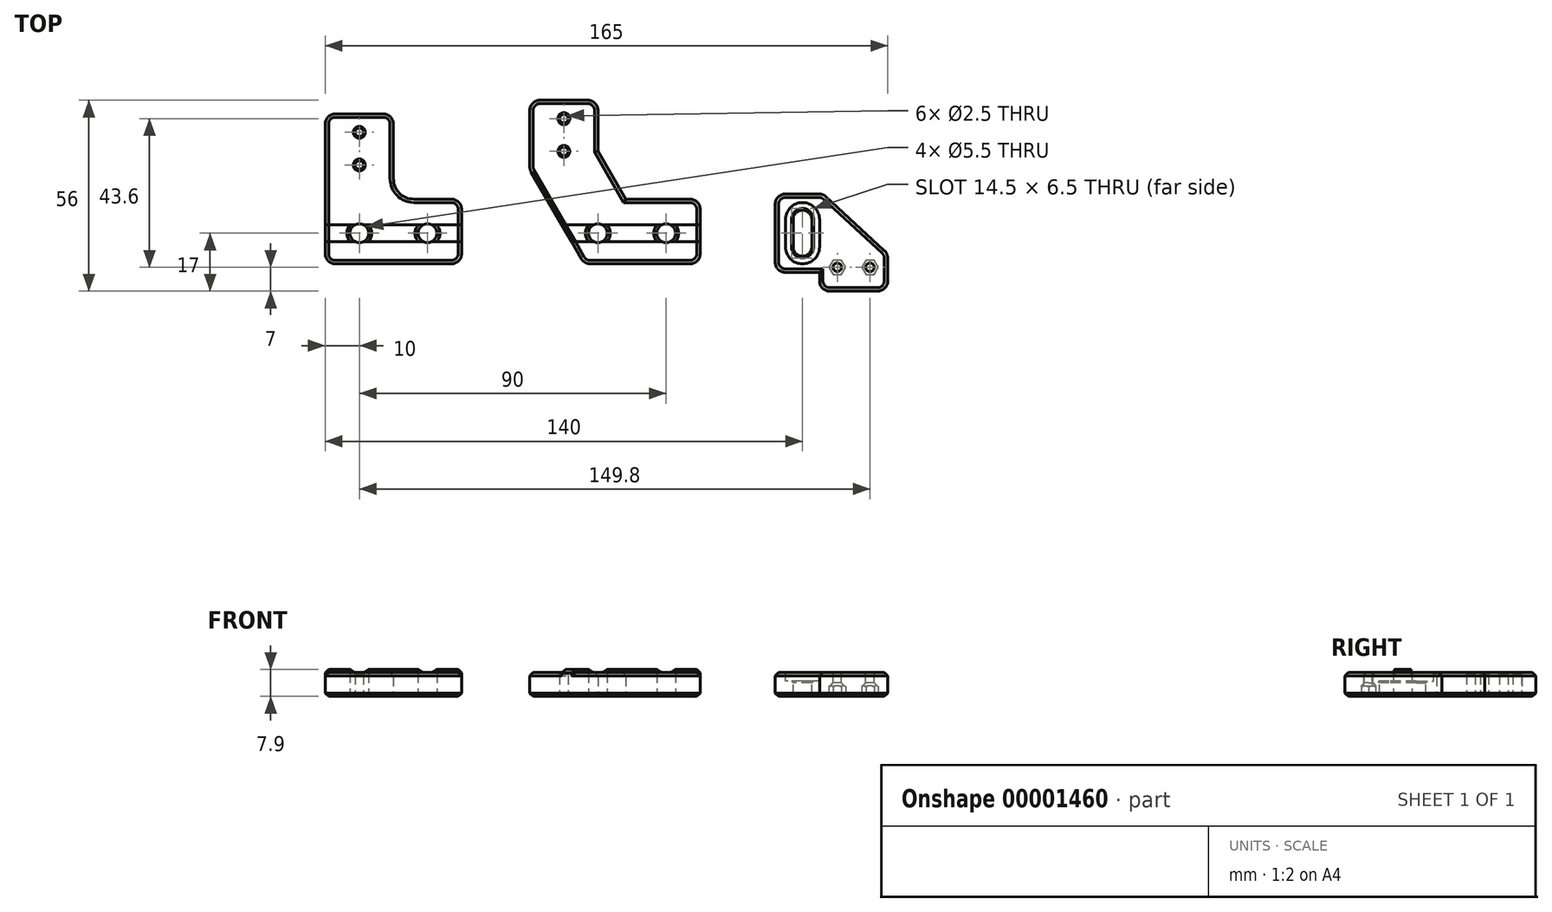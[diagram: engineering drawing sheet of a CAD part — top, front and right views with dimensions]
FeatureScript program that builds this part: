
annotation { "Feature Type Name" : "Feature", "Feature Type Description" : "" }
export const myFeature = defineFeature(function(context is Context, id is Id, definition is map)
    precondition{}
    {
        {
            var Q0;
            Q0=qCreatedBy(makeId("Top.planeOp"),FACE);
            var sketch = newSketch(context, id + "F0", { "sketchPlane" : qUnion([Q0])});
            skLineSegment(sketch, "E0", {"start": v(-8, 11.5) * mm, "end": v(6, 11.5) * mm});
            skLineSegment(sketch, "E1", {"start": v(-8, 11.5) * mm, "end": v(-8, -11.5) * mm});
            skLineSegment(sketch, "E2", {"start": v(5, -11.5) * mm, "end": v(-8, -11.5) * mm});
            skLineSegment(sketch, "E3", {"start": v(5, -11.5) * mm, "end": v(5, -17) * mm});
            skLineSegment(sketch, "E4", {"start": v(25, -17) * mm, "end": v(5, -17) * mm});
            skLineSegment(sketch, "E5", {"start": v(25, -17) * mm, "end": v(25, -6) * mm});
            skLineSegment(sketch, "E6", {"start": v(6, 11.5) * mm, "end": v(25, -6) * mm});
            skLineSegment(sketch, "E7", {"start": v(0, 11.5) * mm, "end": v(0, -11.5) * mm, "construction": true});
            skSolve(sketch);
        }
        {
            var Q0;
            Q0=makeQuery(id+"F0.imprint","IMPRINT",FACE,{"disambiguationData":[TD([[makeQuery(id+"F0.imprint","IMPRINT",EDGE,{"derivedFrom":sQuery(id+"F0.wireOp",EDGE,"E0")}),-1.0]])]});
            extrude(context, id + "F1", {"entities" : qUnion([Q0]), "depth" : 7 * mm});
        }
        {
            var Q0;
            Q0=makeQuery(id+"F1.opExtrude","CAP_FACE",FACE,{"disambiguationData":[OSD([sQuery(id+"F0.wireOp",EDGE,"E0"),sQuery(id+"F0.wireOp",EDGE,"E1"),sQuery(id+"F0.wireOp",EDGE,"E2"),sQuery(id+"F0.wireOp",EDGE,"E3"),sQuery(id+"F0.wireOp",EDGE,"E4"),sQuery(id+"F0.wireOp",EDGE,"E5"),sQuery(id+"F0.wireOp",EDGE,"E6")])],"isStart":false});
            var sketch = newSketch(context, id + "F2", { "sketchPlane" : qUnion([Q0])});
            skLineSegment(sketch, "E8", {"start": v(0, 4) * mm, "end": v(0, -4) * mm, "construction": true});
            skArc(sketch, "E9", {"start": v(2.75, 4) * mm, "mid": v(0, 6.75) * mm, "end": v(-2.75, 4) * mm});
            skArc(sketch, "E10", {"start": v(-2.75, -4) * mm, "mid": v(0, -6.75) * mm, "end": v(2.75, -4) * mm});
            skLineSegment(sketch, "E11", {"start": v(-2.75, 4) * mm, "end": v(-2.75, -4) * mm});
            skLineSegment(sketch, "E12", {"start": v(2.75, 4) * mm, "end": v(2.75, -4) * mm});
            skSolve(sketch);
        }
        {
            var Q0;
            Q0=makeQuery(id+"F2.imprint","IMPRINT",FACE,{"disambiguationData":[TD([[makeQuery(id+"F2.imprint","IMPRINT",EDGE,{"derivedFrom":sQuery(id+"F2.wireOp",EDGE,"E9")}),1.0]])]});
            extrude(context, id + "F3", {"entities" : qUnion([Q0]), "operationType" : NewBodyOperationType.REMOVE, "endBound" : BoundingType.THROUGH_ALL, "oppositeDirection" : true, "depth" : 25 * mm});
        }
        {
            var Q0;
            Q0=makeQuery(id+"F1.opExtrude","CAP_FACE",FACE,{"disambiguationData":[OSD([sQuery(id+"F0.wireOp",EDGE,"E0"),sQuery(id+"F0.wireOp",EDGE,"E1"),sQuery(id+"F0.wireOp",EDGE,"E2"),sQuery(id+"F0.wireOp",EDGE,"E3"),sQuery(id+"F0.wireOp",EDGE,"E4"),sQuery(id+"F0.wireOp",EDGE,"E5"),sQuery(id+"F0.wireOp",EDGE,"E6")])],"isStart":false});
            var sketch = newSketch(context, id + "F4", { "sketchPlane" : qUnion([Q0])});
            skArc(sketch, "E13.0", {"start": v(5, 4) * mm, "mid": v(0, 9) * mm, "end": v(-5, 4) * mm});
            skLineSegment(sketch, "E13.1", {"start": v(5, 4) * mm, "end": v(5, -4) * mm});
            skArc(sketch, "E13.2", {"start": v(-5, -4) * mm, "mid": v(0, -9) * mm, "end": v(5, -4) * mm});
            skLineSegment(sketch, "E13.3", {"start": v(-5, 4) * mm, "end": v(-5, -4) * mm});
            skSolve(sketch);
        }
        {
            var Q0;
            {var subQ3=makeQuery(id+"F4.imprint","IMPRINT",EDGE,{"derivedFrom":makeQuery(id+"F3.boolean.opBoolean","COPY",EDGE,{"derivedFrom":makeQuery(id+"F3.opExtrude","CAP_EDGE",EDGE,{"disambiguationData":[OSD([sQuery(id+"F2.wireOp",EDGE,"E9")])],"isStart":true})})});Q0=qUnion([makeQuery(id+"F4.imprint","IMPRINT",FACE,{"disambiguationData":[TD([[subQ3,1.0]])]}),makeQuery(id+"F4.imprint","IMPRINT",FACE,{"disambiguationData":[TD([[makeQuery(id+"F4.imprint","IMPRINT",EDGE,{"derivedFrom":sQuery(id+"F4.wireOp",EDGE,"E13.0")}),1.0]])]})]);}
            extrude(context, id + "F5", {"entities" : qUnion([Q0]), "operationType" : NewBodyOperationType.REMOVE, "oppositeDirection" : true, "depth" : 2.5 * mm});
        }
        {
            var Q0;
            Q0=makeQuery(id+"F1.opExtrude","CAP_FACE",FACE,{"disambiguationData":[OSD([sQuery(id+"F0.wireOp",EDGE,"E0"),sQuery(id+"F0.wireOp",EDGE,"E1"),sQuery(id+"F0.wireOp",EDGE,"E2"),sQuery(id+"F0.wireOp",EDGE,"E3"),sQuery(id+"F0.wireOp",EDGE,"E4"),sQuery(id+"F0.wireOp",EDGE,"E5"),sQuery(id+"F0.wireOp",EDGE,"E6")])],"isStart":false});
            var sketch = newSketch(context, id + "F6", { "sketchPlane" : qUnion([Q0])});
            skCircle(sketch, "E14", {"center": v(10.2, -10) * mm, "radius": 1.25 * mm});
            skLineSegment(sketch, "E15", {"start": v(10.2, -10) * mm, "end": v(19.8, -10) * mm, "construction": true});
            skCircle(sketch, "E16", {"center": v(19.8, -10) * mm, "radius": 1.25 * mm});
            skLineSegment(sketch, "E17", {"start": v(15, -10) * mm, "end": v(15, -17) * mm, "construction": true});
            skSolve(sketch);
        }
        {
            var Q0;
            {Q0=qUnion([makeQuery(id+"F6.imprint","IMPRINT",FACE,{"disambiguationData":[TD([[makeQuery(id+"F6.imprint","IMPRINT",EDGE,{"derivedFrom":sQuery(id+"F6.wireOp",EDGE,"E14")}),1.0]])]}),makeQuery(id+"F6.imprint","IMPRINT",FACE,{"disambiguationData":[TD([[makeQuery(id+"F6.imprint","IMPRINT",EDGE,{"derivedFrom":sQuery(id+"F6.wireOp",EDGE,"E16")}),1.0]])]})]);}
            extrude(context, id + "F7", {"entities" : qUnion([Q0]), "operationType" : NewBodyOperationType.REMOVE, "endBound" : BoundingType.THROUGH_ALL, "oppositeDirection" : true, "depth" : 25 * mm});
        }
        {
            var Q0;
            Q0=makeQuery(id+"F1.opExtrude","SWEPT_EDGE",EDGE,{"disambiguationData":[OSD([sQuery(id+"F0.wireOp",EDGE,"E1"),sQuery(id+"F0.wireOp",EDGE,"E2")])]});
            var Q1;
            Q1=makeQuery(id+"F1.opExtrude","SWEPT_EDGE",EDGE,{"disambiguationData":[OSD([sQuery(id+"F0.wireOp",EDGE,"E3"),sQuery(id+"F0.wireOp",EDGE,"E4")])]});
            var Q2;
            Q2=makeQuery(id+"F1.opExtrude","SWEPT_EDGE",EDGE,{"disambiguationData":[OSD([sQuery(id+"F0.wireOp",EDGE,"E4"),sQuery(id+"F0.wireOp",EDGE,"E5")])]});
            var Q3;
            Q3=makeQuery(id+"F1.opExtrude","SWEPT_EDGE",EDGE,{"disambiguationData":[OSD([sQuery(id+"F0.wireOp",EDGE,"E5"),sQuery(id+"F0.wireOp",EDGE,"E6")])]});
            var Q4;
            Q4=makeQuery(id+"F1.opExtrude","SWEPT_EDGE",EDGE,{"disambiguationData":[OSD([sQuery(id+"F0.wireOp",EDGE,"E0"),sQuery(id+"F0.wireOp",EDGE,"E6")])]});
            var Q5;
            Q5=makeQuery(id+"F1.opExtrude","SWEPT_EDGE",EDGE,{"disambiguationData":[OSD([sQuery(id+"F0.wireOp",EDGE,"E0"),sQuery(id+"F0.wireOp",EDGE,"E1")])]});
            fillet(context, id + "F8", {"entities" : qUnion([Q0, Q1, Q2, Q3, Q4, Q5]), "radius" : 3 * mm, "tangentPropagation" : true, "allowEdgeOverflow" : false});
        }
        {
            var Q0;
            Q0=makeQuery(id+"F1.opExtrude","SWEPT_BODY",BODY,{"disambiguationData":[OSD([sQuery(id+"F0.wireOp",EDGE,"E0"),sQuery(id+"F0.wireOp",EDGE,"E1"),sQuery(id+"F0.wireOp",EDGE,"E2"),sQuery(id+"F0.wireOp",EDGE,"E3"),sQuery(id+"F0.wireOp",EDGE,"E4"),sQuery(id+"F0.wireOp",EDGE,"E5"),sQuery(id+"F0.wireOp",EDGE,"E6")])]});
            transform(context, id + "F9", {"entities" : qUnion([Q0]), "transformType" : TransformType.TRANSLATION_3D, "dx" : 50 * mm, "dy" : 0 * mm, "dz" : 0 * mm, "makeCopy" : false});
        }
        {
            var Q0;
            Q0=qCreatedBy(makeId("Top.planeOp"),FACE);
            var sketch = newSketch(context, id + "F10", { "sketchPlane" : qUnion([Q0])});
            skLineSegment(sketch, "E18", {"start": v(20, -9) * mm, "end": v(20, 10) * mm});
            skLineSegment(sketch, "E19", {"start": v(20, 10) * mm, "end": v(-1.88, 10) * mm});
            skLineSegment(sketch, "E20", {"start": v(-1.88, 10) * mm, "end": v(-10, 24.07) * mm});
            skLineSegment(sketch, "E21", {"start": v(-10, 24.07) * mm, "end": v(-10, 39) * mm});
            skLineSegment(sketch, "E22", {"start": v(-10, 39) * mm, "end": v(-30, 39) * mm});
            skLineSegment(sketch, "E23", {"start": v(-30, 39) * mm, "end": v(-30, 18.71) * mm});
            skLineSegment(sketch, "E24", {"start": v(-30, 18.71) * mm, "end": v(-14, -9) * mm});
            skLineSegment(sketch, "E25", {"start": v(-14, -9) * mm, "end": v(20, -9) * mm});
            skLineSegment(sketch, "E26", {"start": v(-10, 0) * mm, "end": v(10, 0) * mm, "construction": true});
            skSolve(sketch);
        }
        {
            var Q0;
            Q0=makeQuery(id+"F10.imprint","IMPRINT",FACE,{"disambiguationData":[TD([[makeQuery(id+"F10.imprint","IMPRINT",EDGE,{"derivedFrom":sQuery(id+"F10.wireOp",EDGE,"E18")}),1.0]])]});
            extrude(context, id + "F11", {"entities" : qUnion([Q0]), "depth" : 7 * mm});
        }
        {
            var Q0;
            Q0=makeQuery(id+"F11.opExtrude","SWEPT_FACE",FACE,{"disambiguationData":[OSD([sQuery(id+"F10.wireOp",EDGE,"E18")])]});
            var sketch = newSketch(context, id + "F12", { "sketchPlane" : qUnion([Q0])});
            skLineSegment(sketch, "E27", {"start": v(0, 0) * mm, "end": v(0, 7.45) * mm, "construction": true});
            skLineSegment(sketch, "E28.rect.bottom", {"start": v(2.5, 7) * mm, "end": v(-2.5, 7) * mm});
            skLineSegment(sketch, "E28.rect.top", {"start": v(2.5, 7.9) * mm, "end": v(-2.5, 7.9) * mm});
            skLineSegment(sketch, "E28.rect.left", {"start": v(2.5, 7) * mm, "end": v(2.5, 7.9) * mm});
            skLineSegment(sketch, "E28.rect.right", {"start": v(-2.5, 7) * mm, "end": v(-2.5, 7.9) * mm});
            skPoint(sketch, "E28.rect.middle", {"position": v(0, 7.45) * mm});
            skSolve(sketch);
        }
        {
            var Q0;
            Q0=makeQuery(id+"F12.imprint","IMPRINT",FACE,{"disambiguationData":[TD([[makeQuery(id+"F12.imprint","IMPRINT",EDGE,{"derivedFrom":sQuery(id+"F12.wireOp",EDGE,"E28.rect.bottom")}),1.0]])]});
            var Q1;
            Q1=makeQuery(id+"F11.opExtrude","SWEPT_FACE",FACE,{"disambiguationData":[OSD([sQuery(id+"F10.wireOp",EDGE,"E24")])]});
            extrude(context, id + "F13", {"entities" : qUnion([Q0]), "operationType" : NewBodyOperationType.ADD, "endBound" : BoundingType.UP_TO_SURFACE, "oppositeDirection" : true, "endBoundEntityFace" : qUnion([Q1]), "depth" : 25 * mm});
        }
        {
            var Q0;
            Q0=makeQuery(id+"F11.opExtrude","CAP_FACE",FACE,{"disambiguationData":[OSD([sQuery(id+"F10.wireOp",EDGE,"E18"),sQuery(id+"F10.wireOp",EDGE,"E19"),sQuery(id+"F10.wireOp",EDGE,"E20"),sQuery(id+"F10.wireOp",EDGE,"E21"),sQuery(id+"F10.wireOp",EDGE,"E22"),sQuery(id+"F10.wireOp",EDGE,"E23"),sQuery(id+"F10.wireOp",EDGE,"E24"),sQuery(id+"F10.wireOp",EDGE,"E25")])],"isStart":true});
            var sketch = newSketch(context, id + "F14", { "sketchPlane" : qUnion([Q0])});
            skLineSegment(sketch, "E29", {"start": v(-10, 0) * mm, "end": v(10, 0) * mm, "construction": true});
            skCircle(sketch, "E30", {"center": v(-10, 0) * mm, "radius": 2.75 * mm});
            skCircle(sketch, "E31", {"center": v(10, 0) * mm, "radius": 2.75 * mm});
            skLineSegment(sketch, "E32", {"start": v(-20, -24) * mm, "end": v(-20, -33.6) * mm, "construction": true});
            skCircle(sketch, "E33", {"center": v(-20, -33.6) * mm, "radius": 1.25 * mm});
            skCircle(sketch, "E34", {"center": v(-20, -24) * mm, "radius": 1.25 * mm});
            skLineSegment(sketch, "E35", {"start": v(-20, -39) * mm, "end": v(-20, -33.6) * mm, "construction": true});
            skLineSegment(sketch, "E36", {"start": v(-20, -28.8) * mm, "end": v(-30, -28.8) * mm, "construction": true});
            skSolve(sketch);
        }
        {
            var Q0;
            {Q0=qUnion([makeQuery(id+"F14.imprint","IMPRINT",FACE,{"disambiguationData":[TD([[makeQuery(id+"F14.imprint","IMPRINT",EDGE,{"derivedFrom":sQuery(id+"F14.wireOp",EDGE,"E30")}),1.0]])]}),makeQuery(id+"F14.imprint","IMPRINT",FACE,{"disambiguationData":[TD([[makeQuery(id+"F14.imprint","IMPRINT",EDGE,{"derivedFrom":sQuery(id+"F14.wireOp",EDGE,"E31")}),1.0]])]}),makeQuery(id+"F14.imprint","IMPRINT",FACE,{"disambiguationData":[TD([[makeQuery(id+"F14.imprint","IMPRINT",EDGE,{"derivedFrom":sQuery(id+"F14.wireOp",EDGE,"E33")}),1.0]])]}),makeQuery(id+"F14.imprint","IMPRINT",FACE,{"disambiguationData":[TD([[makeQuery(id+"F14.imprint","IMPRINT",EDGE,{"derivedFrom":sQuery(id+"F14.wireOp",EDGE,"E34")}),1.0]])]})]);}
            extrude(context, id + "F15", {"entities" : qUnion([Q0]), "operationType" : NewBodyOperationType.REMOVE, "endBound" : BoundingType.THROUGH_ALL, "oppositeDirection" : true, "depth" : 25 * mm});
        }
        {
            var Q0;
            Q0=makeQuery(id+"F11.opExtrude","SWEPT_EDGE",EDGE,{"disambiguationData":[OSD([sQuery(id+"F10.wireOp",EDGE,"E24"),sQuery(id+"F10.wireOp",EDGE,"E25")])]});
            var Q1;
            Q1=makeQuery(id+"F11.opExtrude","SWEPT_EDGE",EDGE,{"disambiguationData":[OSD([sQuery(id+"F10.wireOp",EDGE,"E23"),sQuery(id+"F10.wireOp",EDGE,"E24")])]});
            var Q2;
            Q2=makeQuery(id+"F11.opExtrude","SWEPT_EDGE",EDGE,{"disambiguationData":[OSD([sQuery(id+"F10.wireOp",EDGE,"E22"),sQuery(id+"F10.wireOp",EDGE,"E23")])]});
            var Q3;
            Q3=makeQuery(id+"F11.opExtrude","SWEPT_EDGE",EDGE,{"disambiguationData":[OSD([sQuery(id+"F10.wireOp",EDGE,"E21"),sQuery(id+"F10.wireOp",EDGE,"E22")])]});
            var Q4;
            Q4=makeQuery(id+"F11.opExtrude","SWEPT_EDGE",EDGE,{"disambiguationData":[OSD([sQuery(id+"F10.wireOp",EDGE,"E18"),sQuery(id+"F10.wireOp",EDGE,"E19")])]});
            var Q5;
            Q5=makeQuery(id+"F11.opExtrude","SWEPT_EDGE",EDGE,{"disambiguationData":[OSD([sQuery(id+"F10.wireOp",EDGE,"E18"),sQuery(id+"F10.wireOp",EDGE,"E25")])]});
            fillet(context, id + "F16", {"entities" : qUnion([Q0, Q1, Q2, Q3, Q4, Q5]), "radius" : 3 * mm, "tangentPropagation" : true, "allowEdgeOverflow" : false});
        }
        {
            var Q0;
            Q0=makeQuery(id+"F11.opExtrude","SWEPT_BODY",BODY,{"disambiguationData":[OSD([sQuery(id+"F10.wireOp",EDGE,"E18"),sQuery(id+"F10.wireOp",EDGE,"E19"),sQuery(id+"F10.wireOp",EDGE,"E20"),sQuery(id+"F10.wireOp",EDGE,"E21"),sQuery(id+"F10.wireOp",EDGE,"E22"),sQuery(id+"F10.wireOp",EDGE,"E23"),sQuery(id+"F10.wireOp",EDGE,"E24"),sQuery(id+"F10.wireOp",EDGE,"E25")])]});
            var Q1;
            Q1=makeQuery(id+"F1.opExtrude","SWEPT_BODY",BODY,{"disambiguationData":[OSD([sQuery(id+"F0.wireOp",EDGE,"E0"),sQuery(id+"F0.wireOp",EDGE,"E1"),sQuery(id+"F0.wireOp",EDGE,"E2"),sQuery(id+"F0.wireOp",EDGE,"E3"),sQuery(id+"F0.wireOp",EDGE,"E4"),sQuery(id+"F0.wireOp",EDGE,"E5"),sQuery(id+"F0.wireOp",EDGE,"E6")])]});
            transform(context, id + "F17", {"entities" : qUnion([Q0, Q1]), "transformType" : TransformType.TRANSLATION_3D, "dx" : 70 * mm, "dy" : 0 * mm, "dz" : 0 * mm, "makeCopy" : false});
        }
        {
            var Q0;
            Q0=qCreatedBy(makeId("Top.planeOp"),FACE);
            var sketch = newSketch(context, id + "F18", { "sketchPlane" : qUnion([Q0])});
            skLineSegment(sketch, "E37", {"start": v(-10, 0) * mm, "end": v(10, 0) * mm, "construction": true});
            skLineSegment(sketch, "E38", {"start": v(20, -9) * mm, "end": v(20, 10) * mm});
            skLineSegment(sketch, "E39", {"start": v(20, 10) * mm, "end": v(0, 10) * mm});
            skLineSegment(sketch, "E40", {"start": v(0, 10) * mm, "end": v(0, 35) * mm});
            skLineSegment(sketch, "E41", {"start": v(0, 35) * mm, "end": v(-20, 35) * mm});
            skLineSegment(sketch, "E42", {"start": v(-20, 35) * mm, "end": v(-20, -9) * mm});
            skLineSegment(sketch, "E43", {"start": v(-20, -9) * mm, "end": v(20, -9) * mm});
            skSolve(sketch);
        }
        {
            var Q0;
            Q0=makeQuery(id+"F18.imprint","IMPRINT",FACE,{"disambiguationData":[TD([[makeQuery(id+"F18.imprint","IMPRINT",EDGE,{"derivedFrom":sQuery(id+"F18.wireOp",EDGE,"E38")}),1.0]])]});
            var Q1;
            {var subQ0=sQuery(id+"F10.wireOp",EDGE,"E18");var subQ1=sQuery(id+"F10.wireOp",EDGE,"E19");var subQ2=sQuery(id+"F10.wireOp",EDGE,"E20");var subQ3=sQuery(id+"F10.wireOp",EDGE,"E21");var subQ4=sQuery(id+"F10.wireOp",EDGE,"E22");var subQ5=sQuery(id+"F10.wireOp",EDGE,"E23");var subQ6=sQuery(id+"F10.wireOp",EDGE,"E24");Q1=makeQuery(id+"F13.boolean.opBoolean","SPLIT",FACE,{"disambiguationData":[TD([makeQuery(id+"F11.opExtrude","SWEPT_FACE",FACE,{"disambiguationData":[OSD([subQ1])]})])],"derivedFrom":makeQuery(id+"F11.opExtrude","CAP_FACE",FACE,{"disambiguationData":[OSD([subQ0,subQ1,subQ2,subQ3,subQ4,subQ5,subQ6,sQuery(id+"F10.wireOp",EDGE,"E25")])],"isStart":false})});}
            extrude(context, id + "F19", {"entities" : qUnion([Q0]), "endBound" : BoundingType.UP_TO_SURFACE, "endBoundEntityFace" : qUnion([Q1]), "depth" : 25 * mm});
        }
        {
            var Q0;
            Q0=makeQuery(id+"F19.opExtrude","SWEPT_FACE",FACE,{"disambiguationData":[OSD([sQuery(id+"F18.wireOp",EDGE,"E38")])]});
            var sketch = newSketch(context, id + "F20", { "sketchPlane" : qUnion([Q0])});
            skLineSegment(sketch, "E44.0", {"start": v(-2.5, 7) * mm, "end": v(-2.5, 7.9) * mm});
            skLineSegment(sketch, "E45.0", {"start": v(2.5, 7.9) * mm, "end": v(-2.5, 7.9) * mm});
            skLineSegment(sketch, "E46.0", {"start": v(2.5, 7) * mm, "end": v(2.5, 7.9) * mm});
            skLineSegment(sketch, "E47", {"start": v(-2.5, 7) * mm, "end": v(2.5, 7) * mm});
            skSolve(sketch);
        }
        {
            var Q0;
            Q0=makeQuery(id+"F20.imprint","IMPRINT",FACE,{"disambiguationData":[TD([[makeQuery(id+"F20.imprint","IMPRINT",EDGE,{"derivedFrom":sQuery(id+"F20.wireOp",EDGE,"E44.0")}),-1.0]])]});
            var Q1;
            Q1=makeQuery(id+"F19.opExtrude","SWEPT_FACE",FACE,{"disambiguationData":[OSD([sQuery(id+"F18.wireOp",EDGE,"E42")])]});
            extrude(context, id + "F21", {"entities" : qUnion([Q0]), "operationType" : NewBodyOperationType.ADD, "endBound" : BoundingType.UP_TO_SURFACE, "oppositeDirection" : true, "endBoundEntityFace" : qUnion([Q1]), "depth" : 25 * mm});
        }
        {
            var Q0;
            Q0=makeQuery(id+"F19.opExtrude","CAP_FACE",FACE,{"disambiguationData":[OSD([sQuery(id+"F18.wireOp",EDGE,"E38"),sQuery(id+"F18.wireOp",EDGE,"E39"),sQuery(id+"F18.wireOp",EDGE,"E40"),sQuery(id+"F18.wireOp",EDGE,"E41"),sQuery(id+"F18.wireOp",EDGE,"E42"),sQuery(id+"F18.wireOp",EDGE,"E43")])],"isStart":true});
            var sketch = newSketch(context, id + "F22", { "sketchPlane" : qUnion([Q0])});
            skLineSegment(sketch, "E48", {"start": v(10, 0) * mm, "end": v(-10, 0) * mm, "construction": true});
            skCircle(sketch, "E49", {"center": v(10, 0) * mm, "radius": 2.75 * mm});
            skCircle(sketch, "E50", {"center": v(-10, 0) * mm, "radius": 2.75 * mm});
            skLineSegment(sketch, "E51", {"start": v(-10, -35) * mm, "end": v(-10, -29.6) * mm, "construction": true});
            skLineSegment(sketch, "E52", {"start": v(-10, -29.6) * mm, "end": v(-10, -20) * mm, "construction": true});
            skCircle(sketch, "E53", {"center": v(-10, -29.6) * mm, "radius": 1.25 * mm});
            skCircle(sketch, "E54", {"center": v(-10, -20) * mm, "radius": 1.25 * mm});
            skSolve(sketch);
        }
        {
            var Q0;
            {Q0=qUnion([makeQuery(id+"F22.imprint","IMPRINT",FACE,{"disambiguationData":[TD([[makeQuery(id+"F22.imprint","IMPRINT",EDGE,{"derivedFrom":sQuery(id+"F22.wireOp",EDGE,"E49")}),1.0]])]}),makeQuery(id+"F22.imprint","IMPRINT",FACE,{"disambiguationData":[TD([[makeQuery(id+"F22.imprint","IMPRINT",EDGE,{"derivedFrom":sQuery(id+"F22.wireOp",EDGE,"E50")}),1.0]])]}),makeQuery(id+"F22.imprint","IMPRINT",FACE,{"disambiguationData":[TD([[makeQuery(id+"F22.imprint","IMPRINT",EDGE,{"derivedFrom":sQuery(id+"F22.wireOp",EDGE,"E53")}),1.0]])]}),makeQuery(id+"F22.imprint","IMPRINT",FACE,{"disambiguationData":[TD([[makeQuery(id+"F22.imprint","IMPRINT",EDGE,{"derivedFrom":sQuery(id+"F22.wireOp",EDGE,"E54")}),1.0]])]})]);}
            extrude(context, id + "F23", {"entities" : qUnion([Q0]), "operationType" : NewBodyOperationType.REMOVE, "endBound" : BoundingType.THROUGH_ALL, "oppositeDirection" : true, "depth" : 25 * mm});
        }
        {
            var Q0;
            Q0=makeQuery(id+"F19.opExtrude","SWEPT_EDGE",EDGE,{"disambiguationData":[OSD([sQuery(id+"F18.wireOp",EDGE,"E38"),sQuery(id+"F18.wireOp",EDGE,"E39")])]});
            var Q1;
            Q1=makeQuery(id+"F19.opExtrude","SWEPT_EDGE",EDGE,{"disambiguationData":[OSD([sQuery(id+"F18.wireOp",EDGE,"E38"),sQuery(id+"F18.wireOp",EDGE,"E43")])]});
            var Q2;
            Q2=makeQuery(id+"F19.opExtrude","SWEPT_EDGE",EDGE,{"disambiguationData":[OSD([sQuery(id+"F18.wireOp",EDGE,"E40"),sQuery(id+"F18.wireOp",EDGE,"E41")])]});
            var Q3;
            Q3=makeQuery(id+"F19.opExtrude","SWEPT_EDGE",EDGE,{"disambiguationData":[OSD([sQuery(id+"F18.wireOp",EDGE,"E41"),sQuery(id+"F18.wireOp",EDGE,"E42")])]});
            var Q4;
            Q4=makeQuery(id+"F19.opExtrude","SWEPT_EDGE",EDGE,{"disambiguationData":[OSD([sQuery(id+"F18.wireOp",EDGE,"E42"),sQuery(id+"F18.wireOp",EDGE,"E43")])]});
            fillet(context, id + "F24", {"entities" : qUnion([Q0, Q1, Q2, Q3, Q4]), "radius" : 3 * mm, "tangentPropagation" : true, "allowEdgeOverflow" : false});
        }
        {
            var Q0;
            Q0=makeQuery(id+"F19.opExtrude","SWEPT_EDGE",EDGE,{"disambiguationData":[OSD([sQuery(id+"F18.wireOp",EDGE,"E39"),sQuery(id+"F18.wireOp",EDGE,"E40")])]});
            fillet(context, id + "F25", {"entities" : qUnion([Q0]), "radius" : 6 * mm, "tangentPropagation" : true, "allowEdgeOverflow" : false});
        }
        {
            var Q0;
            Q0=makeQuery(id+"F1.opExtrude","CAP_FACE",FACE,{"disambiguationData":[OSD([sQuery(id+"F0.wireOp",EDGE,"E0"),sQuery(id+"F0.wireOp",EDGE,"E1"),sQuery(id+"F0.wireOp",EDGE,"E2"),sQuery(id+"F0.wireOp",EDGE,"E3"),sQuery(id+"F0.wireOp",EDGE,"E4"),sQuery(id+"F0.wireOp",EDGE,"E5"),sQuery(id+"F0.wireOp",EDGE,"E6")])],"isStart":true});
            var sketch = newSketch(context, id + "F26", { "sketchPlane" : qUnion([Q0])});
            skCircle(sketch, "E55.cCircle", {"center": v(139.8, 10) * mm, "radius": 2.1 * mm, "construction": true});
            skLineSegment(sketch, "E55.0", {"start": v(141.01, 7.9) * mm, "end": v(138.59, 7.9) * mm});
            skLineSegment(sketch, "E55.1", {"start": v(138.59, 7.9) * mm, "end": v(137.38, 10) * mm});
            skLineSegment(sketch, "E55.2", {"start": v(137.38, 10) * mm, "end": v(138.59, 12.1) * mm});
            skLineSegment(sketch, "E55.3", {"start": v(138.59, 12.1) * mm, "end": v(141.01, 12.1) * mm});
            skLineSegment(sketch, "E55.4", {"start": v(141.01, 12.1) * mm, "end": v(142.22, 10) * mm});
            skLineSegment(sketch, "E55.5", {"start": v(142.22, 10) * mm, "end": v(141.01, 7.9) * mm});
            skPoint(sketch, "E55.0.midPoint", {"position": v(139.8, 7.9) * mm});
            skCircle(sketch, "E56.cCircle", {"center": v(130.2, 10) * mm, "radius": 2.1 * mm, "construction": true});
            skLineSegment(sketch, "E56.0", {"start": v(131.41, 7.9) * mm, "end": v(128.99, 7.9) * mm});
            skLineSegment(sketch, "E56.1", {"start": v(128.99, 7.9) * mm, "end": v(127.78, 10) * mm});
            skLineSegment(sketch, "E56.2", {"start": v(127.78, 10) * mm, "end": v(128.99, 12.1) * mm});
            skLineSegment(sketch, "E56.3", {"start": v(128.99, 12.1) * mm, "end": v(131.41, 12.1) * mm});
            skLineSegment(sketch, "E56.4", {"start": v(131.41, 12.1) * mm, "end": v(132.62, 10) * mm});
            skLineSegment(sketch, "E56.5", {"start": v(132.62, 10) * mm, "end": v(131.41, 7.9) * mm});
            skPoint(sketch, "E56.0.midPoint", {"position": v(130.2, 7.9) * mm});
            skSolve(sketch);
        }
        {
            var Q0;
            {var subQ0=makeQuery(id+"F1.opExtrude","CAP_FACE",FACE,{"disambiguationData":[OSD([sQuery(id+"F0.wireOp",EDGE,"E0"),sQuery(id+"F0.wireOp",EDGE,"E1"),sQuery(id+"F0.wireOp",EDGE,"E2"),sQuery(id+"F0.wireOp",EDGE,"E3"),sQuery(id+"F0.wireOp",EDGE,"E4"),sQuery(id+"F0.wireOp",EDGE,"E5"),sQuery(id+"F0.wireOp",EDGE,"E6")])],"isStart":true});var subQ1=makeQuery(id+"F26.imprint","IMPRINT",EDGE,{"derivedFrom":makeQuery(id+"F7.boolean.opBoolean","INTERSECT",EDGE,{"derivedFrom":[subQ0,makeQuery(id+"F7.opExtrude","SWEPT_FACE",FACE,{"disambiguationData":[OSD([sQuery(id+"F6.wireOp",EDGE,"E14")])]})]})});var subQ2=makeQuery(id+"F26.imprint","IMPRINT",EDGE,{"derivedFrom":makeQuery(id+"F7.boolean.opBoolean","INTERSECT",EDGE,{"derivedFrom":[subQ0,makeQuery(id+"F7.opExtrude","SWEPT_FACE",FACE,{"disambiguationData":[OSD([sQuery(id+"F6.wireOp",EDGE,"E16")])]})]})});Q0=qUnion([makeQuery(id+"F26.imprint","IMPRINT",FACE,{"disambiguationData":[TD([[subQ1,-1.0]])]}),makeQuery(id+"F26.imprint","IMPRINT",FACE,{"disambiguationData":[TD([[subQ2,-1.0]])]}),makeQuery(id+"F26.imprint","IMPRINT",FACE,{"disambiguationData":[TD([[makeQuery(id+"F26.imprint","IMPRINT",EDGE,{"derivedFrom":sQuery(id+"F26.wireOp",EDGE,"E55.0")}),-1.0]])]}),makeQuery(id+"F26.imprint","IMPRINT",FACE,{"disambiguationData":[TD([[makeQuery(id+"F26.imprint","IMPRINT",EDGE,{"derivedFrom":sQuery(id+"F26.wireOp",EDGE,"E56.0")}),-1.0]])]})]);}
            extrude(context, id + "F27", {"entities" : qUnion([Q0]), "operationType" : NewBodyOperationType.REMOVE, "oppositeDirection" : true, "depth" : 3 * mm});
        }
        {
            var Q0;
            Q0=makeQuery(id+"F27.boolean.opBoolean","INTERSECT",EDGE,{"derivedFrom":[makeQuery(id+"F7.boolean.opBoolean","COPY",FACE,{"derivedFrom":makeQuery(id+"F7.opExtrude","SWEPT_FACE",FACE,{"disambiguationData":[OSD([sQuery(id+"F6.wireOp",EDGE,"E14")])]})}),makeQuery(id+"F27.opExtrude","CAP_FACE",FACE,{"disambiguationData":[OSD([sQuery(id+"F26.wireOp",EDGE,"E56.0"),sQuery(id+"F26.wireOp",EDGE,"E56.1"),sQuery(id+"F26.wireOp",EDGE,"E56.2"),sQuery(id+"F26.wireOp",EDGE,"E56.3"),sQuery(id+"F26.wireOp",EDGE,"E56.4"),sQuery(id+"F26.wireOp",EDGE,"E56.5")])],"isStart":false})]});
            var Q1;
            Q1=makeQuery(id+"F27.boolean.opBoolean","INTERSECT",EDGE,{"derivedFrom":[makeQuery(id+"F7.boolean.opBoolean","COPY",FACE,{"derivedFrom":makeQuery(id+"F7.opExtrude","SWEPT_FACE",FACE,{"disambiguationData":[OSD([sQuery(id+"F6.wireOp",EDGE,"E16")])]})}),makeQuery(id+"F27.opExtrude","CAP_FACE",FACE,{"disambiguationData":[OSD([sQuery(id+"F26.wireOp",EDGE,"E55.0"),sQuery(id+"F26.wireOp",EDGE,"E55.1"),sQuery(id+"F26.wireOp",EDGE,"E55.2"),sQuery(id+"F26.wireOp",EDGE,"E55.3"),sQuery(id+"F26.wireOp",EDGE,"E55.4"),sQuery(id+"F26.wireOp",EDGE,"E55.5")])],"isStart":false})]});
            chamfer(context, id + "F28", {"entities" : qUnion([Q0, Q1]), "width" : 1 * mm, "tangentPropagation" : true});
        }
        {
            var Q0;
            Q0=makeQuery(id+"F19.opExtrude","CAP_EDGE",EDGE,{"disambiguationData":[OSD([sQuery(id+"F18.wireOp",EDGE,"E39")])],"isStart":true});
            var Q1;
            Q1=makeQuery(id+"F11.opExtrude","CAP_EDGE",EDGE,{"disambiguationData":[OSD([sQuery(id+"F10.wireOp",EDGE,"E20")])],"isStart":true});
            var Q2;
            Q2=makeQuery(id+"F1.opExtrude","CAP_EDGE",EDGE,{"disambiguationData":[OSD([sQuery(id+"F0.wireOp",EDGE,"E6")])],"isStart":true});
            var Q3;
            Q3=makeQuery(id+"F11.opExtrude","CAP_EDGE",EDGE,{"disambiguationData":[OSD([sQuery(id+"F10.wireOp",EDGE,"E19")])],"isStart":true});
            var Q4;
            Q4=makeQuery(id+"F19.opExtrude","CAP_EDGE",EDGE,{"disambiguationData":[OSD([sQuery(id+"F18.wireOp",EDGE,"E43")])],"isStart":false});
            var Q5;
            {var subQ0=sQuery(id+"F18.wireOp",EDGE,"E42");var subQ2=sQuery(id+"F18.wireOp",EDGE,"E41");Q5=makeQuery(id+"F21.boolean.opBoolean","SPLIT",EDGE,{"disambiguationData":[TD([makeQuery(id+"F19.opExtrude","SWEPT_FACE",FACE,{"disambiguationData":[OSD([subQ2])]})])],"derivedFrom":makeQuery(id+"F19.opExtrude","CAP_EDGE",EDGE,{"disambiguationData":[OSD([subQ0])],"isStart":false})});}
            var Q6;
            Q6=makeQuery(id+"F11.opExtrude","CAP_EDGE",EDGE,{"disambiguationData":[OSD([sQuery(id+"F10.wireOp",EDGE,"E22")])],"isStart":false});
            var Q7;
            Q7=makeQuery(id+"F11.opExtrude","CAP_EDGE",EDGE,{"disambiguationData":[OSD([sQuery(id+"F10.wireOp",EDGE,"E20")])],"isStart":false});
            var Q8;
            Q8=makeQuery(id+"F11.opExtrude","CAP_EDGE",EDGE,{"disambiguationData":[OSD([sQuery(id+"F10.wireOp",EDGE,"E19")])],"isStart":false});
            var Q9;
            Q9=makeQuery(id+"F11.opExtrude","CAP_EDGE",EDGE,{"disambiguationData":[OSD([sQuery(id+"F10.wireOp",EDGE,"E25")])],"isStart":false});
            var Q10;
            Q10=makeQuery(id+"F1.opExtrude","CAP_EDGE",EDGE,{"disambiguationData":[OSD([sQuery(id+"F0.wireOp",EDGE,"E1")])],"isStart":false});
            chamfer(context, id + "F29", {"entities" : qUnion([Q0, Q1, Q2, Q3, Q4, Q5, Q6, Q7, Q8, Q9, Q10]), "width" : 1 * mm, "tangentPropagation" : true});
        }
        {
            var Q0;
            Q0=makeQuery(id+"F13.opExtrude","CAP_EDGE",EDGE,{"disambiguationData":[OSD([sQuery(id+"F12.wireOp",EDGE,"E28.rect.top")])],"isStart":true});
            var Q1;
            Q1=makeQuery(id+"F13.opExtrude","CAP_EDGE",EDGE,{"disambiguationData":[OSD([sQuery(id+"F12.wireOp",EDGE,"E28.rect.top")])],"isStart":false});
            var Q2;
            Q2=makeQuery(id+"F21.opExtrude","CAP_EDGE",EDGE,{"disambiguationData":[OSD([sQuery(id+"F20.wireOp",EDGE,"E45.0")])],"isStart":true});
            var Q3;
            Q3=makeQuery(id+"F21.opExtrude","CAP_EDGE",EDGE,{"disambiguationData":[OSD([sQuery(id+"F20.wireOp",EDGE,"E45.0")])],"isStart":false});
            chamfer(context, id + "F30", {"entities" : qUnion([Q0, Q1, Q2, Q3]), "width" : 1 * mm, "tangentPropagation" : true});
        }
        {
            var Q0;
            Q0=makeQuery(id+"F15.boolean.opBoolean","INTERSECT",EDGE,{"disambiguationData":[OD(1.0)],"derivedFrom":[makeQuery(id+"F13.opExtrude","SWEPT_FACE",FACE,{"disambiguationData":[OSD([sQuery(id+"F12.wireOp",EDGE,"E28.rect.top")])]}),makeQuery(id+"F15.opExtrude","SWEPT_FACE",FACE,{"disambiguationData":[OSD([sQuery(id+"F14.wireOp",EDGE,"E31")])]})]});
            var Q1;
            Q1=makeQuery(id+"F15.boolean.opBoolean","INTERSECT",EDGE,{"disambiguationData":[OD(0.0)],"derivedFrom":[makeQuery(id+"F13.opExtrude","SWEPT_FACE",FACE,{"disambiguationData":[OSD([sQuery(id+"F12.wireOp",EDGE,"E28.rect.top")])]}),makeQuery(id+"F15.opExtrude","SWEPT_FACE",FACE,{"disambiguationData":[OSD([sQuery(id+"F14.wireOp",EDGE,"E31")])]})]});
            var Q2;
            Q2=makeQuery(id+"F15.boolean.opBoolean","INTERSECT",EDGE,{"disambiguationData":[OD(0.0)],"derivedFrom":[makeQuery(id+"F13.opExtrude","SWEPT_FACE",FACE,{"disambiguationData":[OSD([sQuery(id+"F12.wireOp",EDGE,"E28.rect.top")])]}),makeQuery(id+"F15.opExtrude","SWEPT_FACE",FACE,{"disambiguationData":[OSD([sQuery(id+"F14.wireOp",EDGE,"E30")])]})]});
            var Q3;
            Q3=makeQuery(id+"F15.boolean.opBoolean","INTERSECT",EDGE,{"disambiguationData":[OD(1.0)],"derivedFrom":[makeQuery(id+"F13.opExtrude","SWEPT_FACE",FACE,{"disambiguationData":[OSD([sQuery(id+"F12.wireOp",EDGE,"E28.rect.top")])]}),makeQuery(id+"F15.opExtrude","SWEPT_FACE",FACE,{"disambiguationData":[OSD([sQuery(id+"F14.wireOp",EDGE,"E30")])]})]});
            var Q4;
            Q4=makeQuery(id+"F23.boolean.opBoolean","INTERSECT",EDGE,{"disambiguationData":[OD(0.0)],"derivedFrom":[makeQuery(id+"F21.opExtrude","SWEPT_FACE",FACE,{"disambiguationData":[OSD([sQuery(id+"F20.wireOp",EDGE,"E45.0")])]}),makeQuery(id+"F23.opExtrude","SWEPT_FACE",FACE,{"disambiguationData":[OSD([sQuery(id+"F22.wireOp",EDGE,"E49")])]})]});
            var Q5;
            Q5=makeQuery(id+"F23.boolean.opBoolean","INTERSECT",EDGE,{"disambiguationData":[OD(1.0)],"derivedFrom":[makeQuery(id+"F21.opExtrude","SWEPT_FACE",FACE,{"disambiguationData":[OSD([sQuery(id+"F20.wireOp",EDGE,"E45.0")])]}),makeQuery(id+"F23.opExtrude","SWEPT_FACE",FACE,{"disambiguationData":[OSD([sQuery(id+"F22.wireOp",EDGE,"E50")])]})]});
            var Q6;
            Q6=makeQuery(id+"F23.boolean.opBoolean","INTERSECT",EDGE,{"disambiguationData":[OD(0.0)],"derivedFrom":[makeQuery(id+"F21.opExtrude","SWEPT_FACE",FACE,{"disambiguationData":[OSD([sQuery(id+"F20.wireOp",EDGE,"E45.0")])]}),makeQuery(id+"F23.opExtrude","SWEPT_FACE",FACE,{"disambiguationData":[OSD([sQuery(id+"F22.wireOp",EDGE,"E50")])]})]});
            var Q7;
            Q7=makeQuery(id+"F23.boolean.opBoolean","INTERSECT",EDGE,{"disambiguationData":[OD(1.0)],"derivedFrom":[makeQuery(id+"F21.opExtrude","SWEPT_FACE",FACE,{"disambiguationData":[OSD([sQuery(id+"F20.wireOp",EDGE,"E45.0")])]}),makeQuery(id+"F23.opExtrude","SWEPT_FACE",FACE,{"disambiguationData":[OSD([sQuery(id+"F22.wireOp",EDGE,"E49")])]})]});
            chamfer(context, id + "F31", {"entities" : qUnion([Q0, Q1, Q2, Q3, Q4, Q5, Q6, Q7]), "width" : .9 * mm, "tangentPropagation" : true});
        }
        {
            var Q0;
            Q0=makeQuery(id+"F15.boolean.opBoolean","COPY",EDGE,{"derivedFrom":makeQuery(id+"F15.opExtrude","CAP_EDGE",EDGE,{"disambiguationData":[OSD([sQuery(id+"F14.wireOp",EDGE,"E31")])],"isStart":true})});
            var Q1;
            Q1=makeQuery(id+"F15.boolean.opBoolean","COPY",EDGE,{"derivedFrom":makeQuery(id+"F15.opExtrude","CAP_EDGE",EDGE,{"disambiguationData":[OSD([sQuery(id+"F14.wireOp",EDGE,"E30")])],"isStart":true})});
            var Q2;
            Q2=makeQuery(id+"F23.boolean.opBoolean","COPY",EDGE,{"derivedFrom":makeQuery(id+"F23.opExtrude","CAP_EDGE",EDGE,{"disambiguationData":[OSD([sQuery(id+"F22.wireOp",EDGE,"E49")])],"isStart":true})});
            var Q3;
            Q3=makeQuery(id+"F23.boolean.opBoolean","COPY",EDGE,{"derivedFrom":makeQuery(id+"F23.opExtrude","CAP_EDGE",EDGE,{"disambiguationData":[OSD([sQuery(id+"F22.wireOp",EDGE,"E50")])],"isStart":true})});
            var Q4;
            Q4=makeQuery(id+"F3.boolean.opBoolean","INTERSECT",EDGE,{"derivedFrom":[makeQuery(id+"F1.opExtrude","CAP_FACE",FACE,{"disambiguationData":[OSD([sQuery(id+"F0.wireOp",EDGE,"E0"),sQuery(id+"F0.wireOp",EDGE,"E1"),sQuery(id+"F0.wireOp",EDGE,"E2"),sQuery(id+"F0.wireOp",EDGE,"E3"),sQuery(id+"F0.wireOp",EDGE,"E4"),sQuery(id+"F0.wireOp",EDGE,"E5"),sQuery(id+"F0.wireOp",EDGE,"E6")])],"isStart":true}),makeQuery(id+"F3.opExtrude","SWEPT_FACE",FACE,{"disambiguationData":[OSD([sQuery(id+"F2.wireOp",EDGE,"E10")])]})]});
            var Q5;
            Q5=makeQuery(id+"F15.boolean.opBoolean","COPY",EDGE,{"derivedFrom":makeQuery(id+"F15.opExtrude","CAP_EDGE",EDGE,{"disambiguationData":[OSD([sQuery(id+"F14.wireOp",EDGE,"E34")])],"isStart":true})});
            var Q6;
            Q6=makeQuery(id+"F15.boolean.opBoolean","COPY",EDGE,{"derivedFrom":makeQuery(id+"F15.opExtrude","CAP_EDGE",EDGE,{"disambiguationData":[OSD([sQuery(id+"F14.wireOp",EDGE,"E33")])],"isStart":true})});
            var Q7;
            Q7=makeQuery(id+"F23.boolean.opBoolean","COPY",EDGE,{"derivedFrom":makeQuery(id+"F23.opExtrude","CAP_EDGE",EDGE,{"disambiguationData":[OSD([sQuery(id+"F22.wireOp",EDGE,"E54")])],"isStart":true})});
            var Q8;
            Q8=makeQuery(id+"F23.boolean.opBoolean","COPY",EDGE,{"derivedFrom":makeQuery(id+"F23.opExtrude","CAP_EDGE",EDGE,{"disambiguationData":[OSD([sQuery(id+"F22.wireOp",EDGE,"E53")])],"isStart":true})});
            var Q9;
            {var subQ0=sQuery(id+"F10.wireOp",EDGE,"E20");var subQ1=sQuery(id+"F10.wireOp",EDGE,"E19");var subQ6=sQuery(id+"F10.wireOp",EDGE,"E21");var subQ7=sQuery(id+"F10.wireOp",EDGE,"E18");var subQ8=sQuery(id+"F10.wireOp",EDGE,"E22");var subQ9=sQuery(id+"F10.wireOp",EDGE,"E23");var subQ10=sQuery(id+"F10.wireOp",EDGE,"E24");Q9=makeQuery(id+"F15.boolean.opBoolean","INTERSECT",EDGE,{"derivedFrom":[makeQuery(id+"F13.boolean.opBoolean","SPLIT",FACE,{"disambiguationData":[TD([makeQuery(id+"F11.opExtrude","SWEPT_FACE",FACE,{"disambiguationData":[OSD([subQ1])]})])],"derivedFrom":makeQuery(id+"F11.opExtrude","CAP_FACE",FACE,{"disambiguationData":[OSD([subQ7,subQ1,subQ0,subQ6,subQ8,subQ9,subQ10,sQuery(id+"F10.wireOp",EDGE,"E25")])],"isStart":false})}),makeQuery(id+"F15.opExtrude","SWEPT_FACE",FACE,{"disambiguationData":[OSD([sQuery(id+"F14.wireOp",EDGE,"E33")])]})]});}
            var Q10;
            {var subQ0=sQuery(id+"F10.wireOp",EDGE,"E20");var subQ1=sQuery(id+"F10.wireOp",EDGE,"E19");var subQ6=sQuery(id+"F10.wireOp",EDGE,"E21");var subQ7=sQuery(id+"F10.wireOp",EDGE,"E18");var subQ8=sQuery(id+"F10.wireOp",EDGE,"E22");var subQ9=sQuery(id+"F10.wireOp",EDGE,"E23");var subQ10=sQuery(id+"F10.wireOp",EDGE,"E24");Q10=makeQuery(id+"F15.boolean.opBoolean","INTERSECT",EDGE,{"derivedFrom":[makeQuery(id+"F13.boolean.opBoolean","SPLIT",FACE,{"disambiguationData":[TD([makeQuery(id+"F11.opExtrude","SWEPT_FACE",FACE,{"disambiguationData":[OSD([subQ1])]})])],"derivedFrom":makeQuery(id+"F11.opExtrude","CAP_FACE",FACE,{"disambiguationData":[OSD([subQ7,subQ1,subQ0,subQ6,subQ8,subQ9,subQ10,sQuery(id+"F10.wireOp",EDGE,"E25")])],"isStart":false})}),makeQuery(id+"F15.opExtrude","SWEPT_FACE",FACE,{"disambiguationData":[OSD([sQuery(id+"F14.wireOp",EDGE,"E34")])]})]});}
            var Q11;
            {var subQ0=sQuery(id+"F18.wireOp",EDGE,"E40");var subQ1=sQuery(id+"F18.wireOp",EDGE,"E39");var subQ6=sQuery(id+"F18.wireOp",EDGE,"E41");var subQ7=sQuery(id+"F18.wireOp",EDGE,"E38");var subQ8=sQuery(id+"F18.wireOp",EDGE,"E42");Q11=makeQuery(id+"F23.boolean.opBoolean","INTERSECT",EDGE,{"derivedFrom":[makeQuery(id+"F21.boolean.opBoolean","SPLIT",FACE,{"disambiguationData":[TD([makeQuery(id+"F19.opExtrude","SWEPT_FACE",FACE,{"disambiguationData":[OSD([subQ1])]})])],"derivedFrom":makeQuery(id+"F19.opExtrude","CAP_FACE",FACE,{"disambiguationData":[OSD([subQ7,subQ1,subQ0,subQ6,subQ8,sQuery(id+"F18.wireOp",EDGE,"E43")])],"isStart":false})}),makeQuery(id+"F23.opExtrude","SWEPT_FACE",FACE,{"disambiguationData":[OSD([sQuery(id+"F22.wireOp",EDGE,"E53")])]})]});}
            var Q12;
            {var subQ0=sQuery(id+"F18.wireOp",EDGE,"E40");var subQ1=sQuery(id+"F18.wireOp",EDGE,"E39");var subQ6=sQuery(id+"F18.wireOp",EDGE,"E41");var subQ7=sQuery(id+"F18.wireOp",EDGE,"E38");var subQ8=sQuery(id+"F18.wireOp",EDGE,"E42");Q12=makeQuery(id+"F23.boolean.opBoolean","INTERSECT",EDGE,{"derivedFrom":[makeQuery(id+"F21.boolean.opBoolean","SPLIT",FACE,{"disambiguationData":[TD([makeQuery(id+"F19.opExtrude","SWEPT_FACE",FACE,{"disambiguationData":[OSD([subQ1])]})])],"derivedFrom":makeQuery(id+"F19.opExtrude","CAP_FACE",FACE,{"disambiguationData":[OSD([subQ7,subQ1,subQ0,subQ6,subQ8,sQuery(id+"F18.wireOp",EDGE,"E43")])],"isStart":false})}),makeQuery(id+"F23.opExtrude","SWEPT_FACE",FACE,{"disambiguationData":[OSD([sQuery(id+"F22.wireOp",EDGE,"E54")])]})]});}
            var Q13;
            Q13=makeQuery(id+"F7.boolean.opBoolean","COPY",EDGE,{"derivedFrom":makeQuery(id+"F7.opExtrude","CAP_EDGE",EDGE,{"disambiguationData":[OSD([sQuery(id+"F6.wireOp",EDGE,"E14")])],"isStart":true})});
            var Q14;
            Q14=makeQuery(id+"F7.boolean.opBoolean","COPY",EDGE,{"derivedFrom":makeQuery(id+"F7.opExtrude","CAP_EDGE",EDGE,{"disambiguationData":[OSD([sQuery(id+"F6.wireOp",EDGE,"E16")])],"isStart":true})});
            var Q15;
            Q15=makeQuery(id+"F5.boolean.opBoolean","COPY",EDGE,{"derivedFrom":makeQuery(id+"F5.opExtrude","CAP_EDGE",EDGE,{"disambiguationData":[OSD([sQuery(id+"F4.wireOp",EDGE,"E13.3")])],"isStart":true})});
            var Q16;
            Q16=makeQuery(id+"F5.boolean.opBoolean","INTERSECT",EDGE,{"derivedFrom":[makeQuery(id+"F3.boolean.opBoolean","COPY",FACE,{"derivedFrom":makeQuery(id+"F3.opExtrude","SWEPT_FACE",FACE,{"disambiguationData":[OSD([sQuery(id+"F2.wireOp",EDGE,"E11")])]})}),makeQuery(id+"F5.opExtrude","CAP_FACE",FACE,{"disambiguationData":[OSD([sQuery(id+"F4.wireOp",EDGE,"E13.0"),sQuery(id+"F4.wireOp",EDGE,"E13.1"),sQuery(id+"F4.wireOp",EDGE,"E13.2"),sQuery(id+"F4.wireOp",EDGE,"E13.3")])],"isStart":false})]});
            chamfer(context, id + "F32", {"entities" : qUnion([Q0, Q1, Q2, Q3, Q4, Q5, Q6, Q7, Q8, Q9, Q10, Q11, Q12, Q13, Q14, Q15, Q16]), "width" : .5 * mm, "tangentPropagation" : true});
        }
    });
